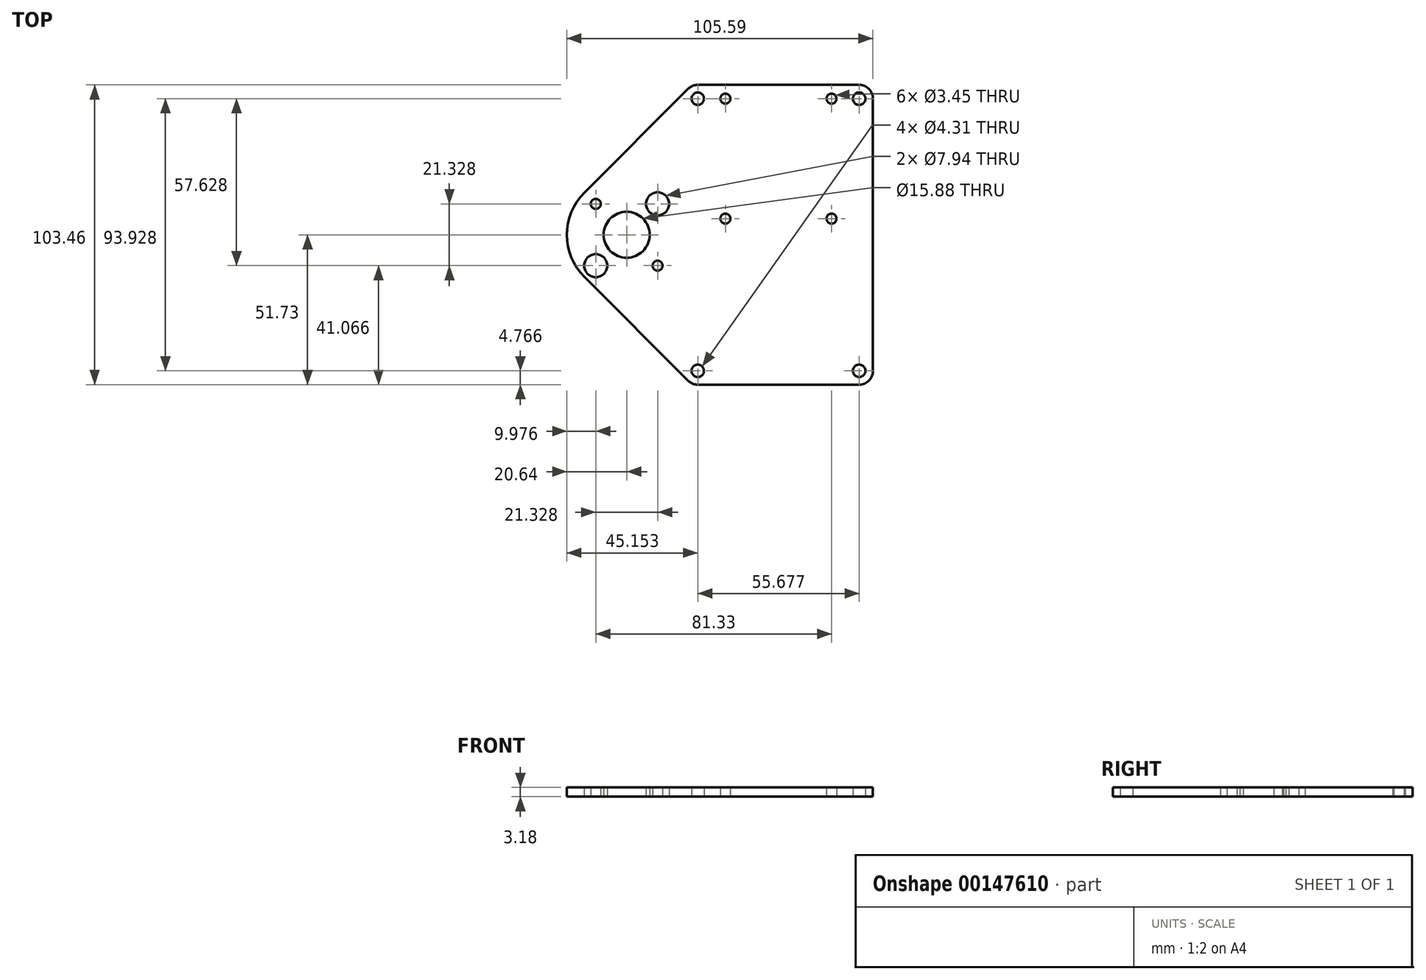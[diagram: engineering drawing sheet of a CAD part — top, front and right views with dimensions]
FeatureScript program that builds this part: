
annotation { "Feature Type Name" : "Feature", "Feature Type Description" : "" }
export const myFeature = defineFeature(function(context is Context, id is Id, definition is map)
    precondition{}
    {
        {
            var Q0;
            Q0=qCreatedBy(makeId("Top.planeOp"),FACE);
            var sketch = newSketch(context, id + "F0", { "sketchPlane" : qUnion([Q0])});
            skPoint(sketch, "E0.rect.middle", {"position": v(0, 0) * mm});
            skCircle(sketch, "E1", {"center": v(0, 0) * mm, "radius": 7.94 * mm});
            skLineSegment(sketch, "E2", {"start": v(0, 0) * mm, "end": v(84.95, 0) * mm, "construction": true});
            skLineSegment(sketch, "E3", {"start": v(84.95, 0) * mm, "end": v(84.95, 0) * mm});
            skLineSegment(sketch, "E4", {"start": v(-14.6, 14.6) * mm, "end": v(21.15, 50.33) * mm});
            skLineSegment(sketch, "E5", {"start": v(-14.6, -14.6) * mm, "end": v(21.15, -50.33) * mm});
            skCircle(sketch, "E6", {"center": v(24.51, 46.96) * mm, "radius": 2.15 * mm});
            skArc(sketch, "E7", {"start": v(24.51, 51.73) * mm, "mid": v(22.7, 51.36) * mm, "end": v(21.15, 50.33) * mm});
            skLineSegment(sketch, "E8", {"start": v(24.51, 51.73) * mm, "end": v(84.95, 51.73) * mm});
            skLineSegment(sketch, "E9", {"start": v(84.95, 51.73) * mm, "end": v(84.95, -51.73) * mm});
            skLineSegment(sketch, "E10", {"start": v(84.95, -51.73) * mm, "end": v(24.51, -51.73) * mm});
            skArc(sketch, "E11", {"start": v(21.15, -50.33) * mm, "mid": v(22.7, -51.36) * mm, "end": v(24.51, -51.73) * mm});
            skLineSegment(sketch, "E12", {"start": v(80.2, 46.96) * mm, "end": v(80.2, 51.73) * mm, "construction": true});
            skLineSegment(sketch, "E13", {"start": v(80.2, 46.96) * mm, "end": v(84.95, 46.96) * mm, "construction": true});
            skLineSegment(sketch, "E14", {"start": v(24.51, 46.96) * mm, "end": v(24.51, 51.73) * mm, "construction": true});
            skCircle(sketch, "E15", {"center": v(80.2, 46.96) * mm, "radius": 2.15 * mm});
            skCircle(sketch, "E16", {"center": v(80.2, -46.96) * mm, "radius": 2.15 * mm});
            skCircle(sketch, "E17", {"center": v(24.51, -46.96) * mm, "radius": 2.15 * mm});
            skArc(sketch, "E18", {"start": v(-14.6, 14.6) * mm, "mid": v(-20.64, 0) * mm, "end": v(-14.6, -14.6) * mm});
            skLineSegment(sketch, "E19", {"start": v(80.2, 46.96) * mm, "end": v(70.67, 46.96) * mm, "construction": true});
            skCircle(sketch, "E20", {"center": v(70.67, 46.96) * mm, "radius": 1.73 * mm});
            skLineSegment(sketch, "E21", {"start": v(24.51, -46.96) * mm, "end": v(80.2, -46.96) * mm, "construction": true});
            skLineSegment(sketch, "E22", {"start": v(70.67, 46.96) * mm, "end": v(70.67, 5.56) * mm, "construction": true});
            skCircle(sketch, "E23", {"center": v(70.67, 5.56) * mm, "radius": 1.73 * mm});
            skLineSegment(sketch, "E24", {"start": v(70.67, 46.96) * mm, "end": v(34.04, 46.96) * mm, "construction": true});
            skLineSegment(sketch, "E25", {"start": v(34.04, 46.96) * mm, "end": v(24.51, 46.96) * mm, "construction": true});
            skLineSegment(sketch, "E26", {"start": v(80.2, 46.96) * mm, "end": v(80.2, -46.96) * mm, "construction": true});
            skLineSegment(sketch, "E27", {"start": v(34.04, 46.96) * mm, "end": v(34.04, 5.56) * mm, "construction": true});
            skCircle(sketch, "E28", {"center": v(34.04, 5.56) * mm, "radius": 1.73 * mm});
            skLineSegment(sketch, "E29.bottom", {"start": v(10.66, -10.66) * mm, "end": v(-10.66, -10.66) * mm, "construction": true});
            skLineSegment(sketch, "E29.top", {"start": v(10.66, 10.66) * mm, "end": v(-10.66, 10.66) * mm, "construction": true});
            skLineSegment(sketch, "E29.left", {"start": v(10.66, -10.66) * mm, "end": v(10.66, 10.66) * mm, "construction": true});
            skLineSegment(sketch, "E29.right", {"start": v(-10.66, -10.66) * mm, "end": v(-10.66, 10.66) * mm, "construction": true});
            skCircle(sketch, "E30", {"center": v(-10.66, 10.66) * mm, "radius": 5.56 * mm, "construction": true});
            skCircle(sketch, "E31", {"center": v(0, 0) * mm, "radius": 9.53 * mm, "construction": true});
            skCircle(sketch, "E32", {"center": v(-10.66, 10.66) * mm, "radius": 1.73 * mm});
            skCircle(sketch, "E33", {"center": v(10.66, 10.66) * mm, "radius": 3.97 * mm});
            skCircle(sketch, "E34", {"center": v(10.66, -10.66) * mm, "radius": 1.73 * mm});
            skCircle(sketch, "E35", {"center": v(-10.66, -10.66) * mm, "radius": 3.97 * mm});
            skCircle(sketch, "E36", {"center": v(34.04, 46.96) * mm, "radius": 1.73 * mm});
            skSolve(sketch);
        }
        {
            var Q0;
            Q0=qSketchRegion(id+"F0",true);
            extrude(context, id + "F1", {"entities" : qUnion([Q0]), "depth" : 3.17 * mm});
        }
        {
            var Q0;
            Q0=makeQuery(id+"F1.opExtrude","SWEPT_EDGE",EDGE,{"disambiguationData":[OSD([sQuery(id+"F0.wireOp",EDGE,"E8"),sQuery(id+"F0.wireOp",EDGE,"E9")])]});
            var Q1;
            Q1=makeQuery(id+"F1.opExtrude","SWEPT_EDGE",EDGE,{"disambiguationData":[OSD([sQuery(id+"F0.wireOp",EDGE,"E9"),sQuery(id+"F0.wireOp",EDGE,"E10")])]});
            fillet(context, id + "F2", {"entities" : qUnion([Q0, Q1]), "radius" : 4.76 * mm, "tangentPropagation" : true, "allowEdgeOverflow" : false});
        }
    });
